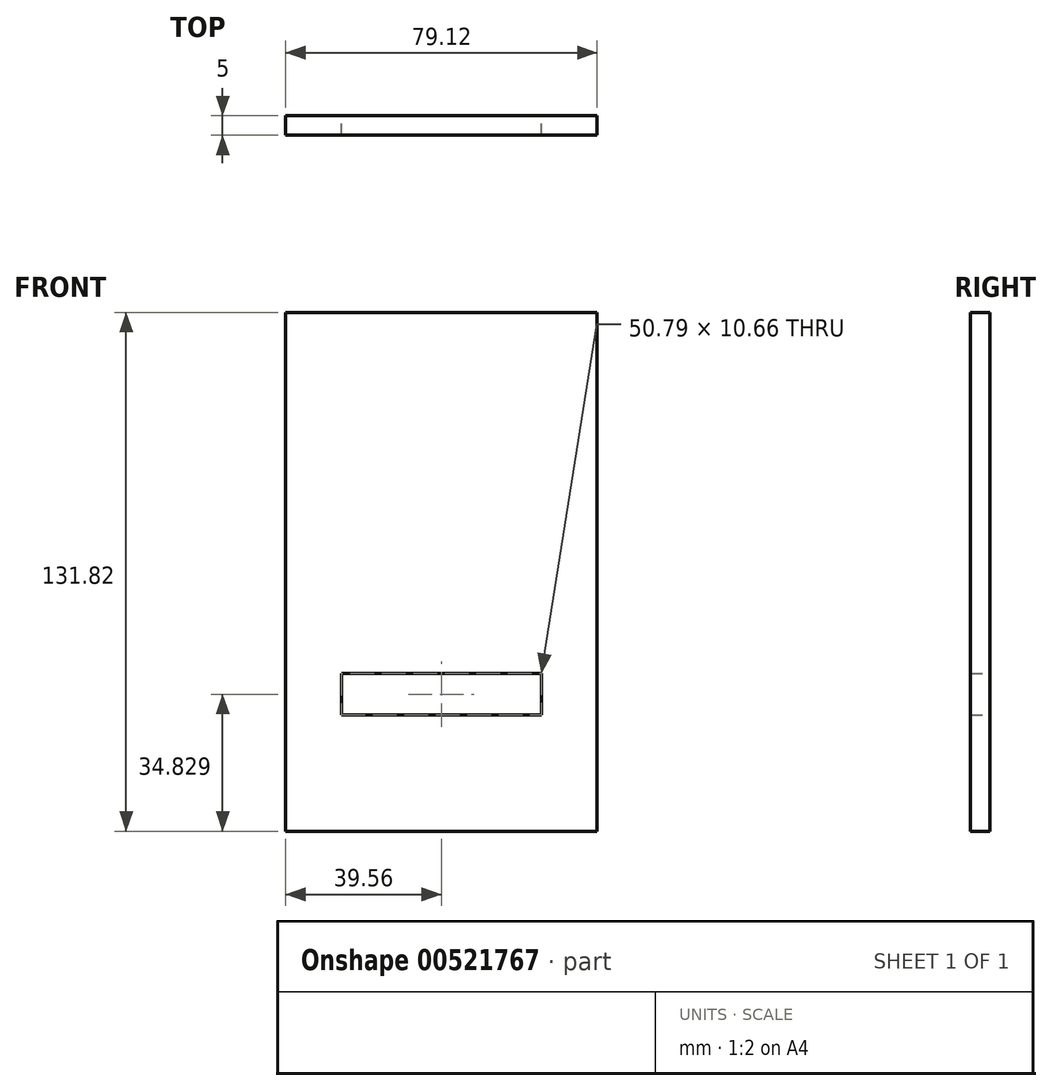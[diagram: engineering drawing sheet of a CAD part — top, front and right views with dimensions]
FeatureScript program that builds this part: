
annotation { "Feature Type Name" : "Feature", "Feature Type Description" : "" }
export const myFeature = defineFeature(function(context is Context, id is Id, definition is map)
    precondition{}
    {
        {
            var Q0;
            Q0=qCreatedBy(makeId("Front.planeOp"),FACE);
            var sketch = newSketch(context, id + "F0", { "sketchPlane" : qUnion([Q0])});
            skLineSegment(sketch, "E0.bottom", {"start": v(39.56, -65.91) * mm, "end": v(-39.56, -65.91) * mm});
            skLineSegment(sketch, "E0.top", {"start": v(39.56, 65.91) * mm, "end": v(-39.56, 65.91) * mm});
            skLineSegment(sketch, "E0.left", {"start": v(39.56, -65.91) * mm, "end": v(39.56, 65.91) * mm});
            skLineSegment(sketch, "E0.right", {"start": v(-39.56, -65.91) * mm, "end": v(-39.56, 65.91) * mm});
            skPoint(sketch, "E0.middle", {"position": v(0, 0) * mm});
            skSolve(sketch);
        }
        {
            var Q0;
            Q0 = qSketchRegion(id + "F0", true);
            extrude(context, id + "F1", {"entities" : qUnion([Q0]), "depth" : 5 * mm, "offsetDistance" : 25 * mm});
        }
        {
            var Q0;
            Q0=makeQuery(id+"F0.imprint","IMPRINT",FACE,{"disambiguationData":[TD([[makeQuery(id+"F0.imprint","IMPRINT",EDGE,{"derivedFrom":sQuery(id+"F0.wireOp",EDGE,"E0.bottom")}),-1.0]])]});
            var sketch = newSketch(context, id + "F2", { "sketchPlane" : qUnion([Q0])});
            skLineSegment(sketch, "E1.bottom", {"start": v(-25.4, -25.75) * mm, "end": v(25.4, -25.75) * mm});
            skLineSegment(sketch, "E1.top", {"start": v(-25.4, -36.4) * mm, "end": v(25.4, -36.4) * mm});
            skLineSegment(sketch, "E1.left", {"start": v(-25.4, -25.75) * mm, "end": v(-25.4, -36.4) * mm});
            skLineSegment(sketch, "E1.right", {"start": v(25.4, -25.75) * mm, "end": v(25.4, -36.4) * mm});
            skPoint(sketch, "E1.middle", {"position": v(0, -31.08) * mm});
            skSolve(sketch);
        }
        {
            var Q0;
            Q0 = qSketchRegion(id + "F2", true);
            extrude(context, id + "F3", {"entities" : qUnion([Q0]), "operationType" : NewBodyOperationType.REMOVE, "depth" : 10 * mm, "offsetDistance" : 25 * mm});
        }
    });
